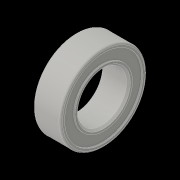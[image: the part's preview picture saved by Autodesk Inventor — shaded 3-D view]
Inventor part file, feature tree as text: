
AUTODESK INVENTOR PART (.ipt)
format: ipt  version: 2016 (Build 200138000, 138)  size: 146,944 bytes
history: native  units: in
note: dims shown in document units (in); Inventor stores cm internally (conversion verified against a paired STEP export)
features: revolve x1
ambient origin geometry x8: Origin, YZ Plane, XZ Plane, XY Plane, X Axis, Y Axis, Z Axis, Center Point
bodies: Solid1 (feature_tree)
feature tree (1):
  revolve  "Revolve1"  [1 undecoded]
note: 1 required parameter value undecoded (feature->parameter linkage not recoverable at this tier; creation-order binding heuristic only, values carry confidence <= 0.55)
